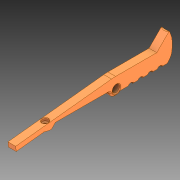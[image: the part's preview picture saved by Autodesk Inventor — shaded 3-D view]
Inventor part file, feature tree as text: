
AUTODESK INVENTOR PART (.ipt)
format: ipt  version: 2020 (Build 240168000, 168)  size: 201,216 bytes
history: native  units: in
note: dims shown in document units (in); Inventor stores cm internally (conversion verified against a paired STEP export)
features: extrude x1, sketch x1, imported_body x1
ambient origin geometry x8: Origin, YZ Plane, XZ Plane, XY Plane, X Axis, Y Axis, Z Axis, Center Point
bodies: Solid1 (feature_tree)
feature tree (3):
  extrude  "Extrusion1"  Depth=0.3937in TaperAngle=0.0deg
  sketch  "Sketch1"  dims[d0=0.9843in d1=0.3937in d2=0.0in]
  imported_body  "Base1"
